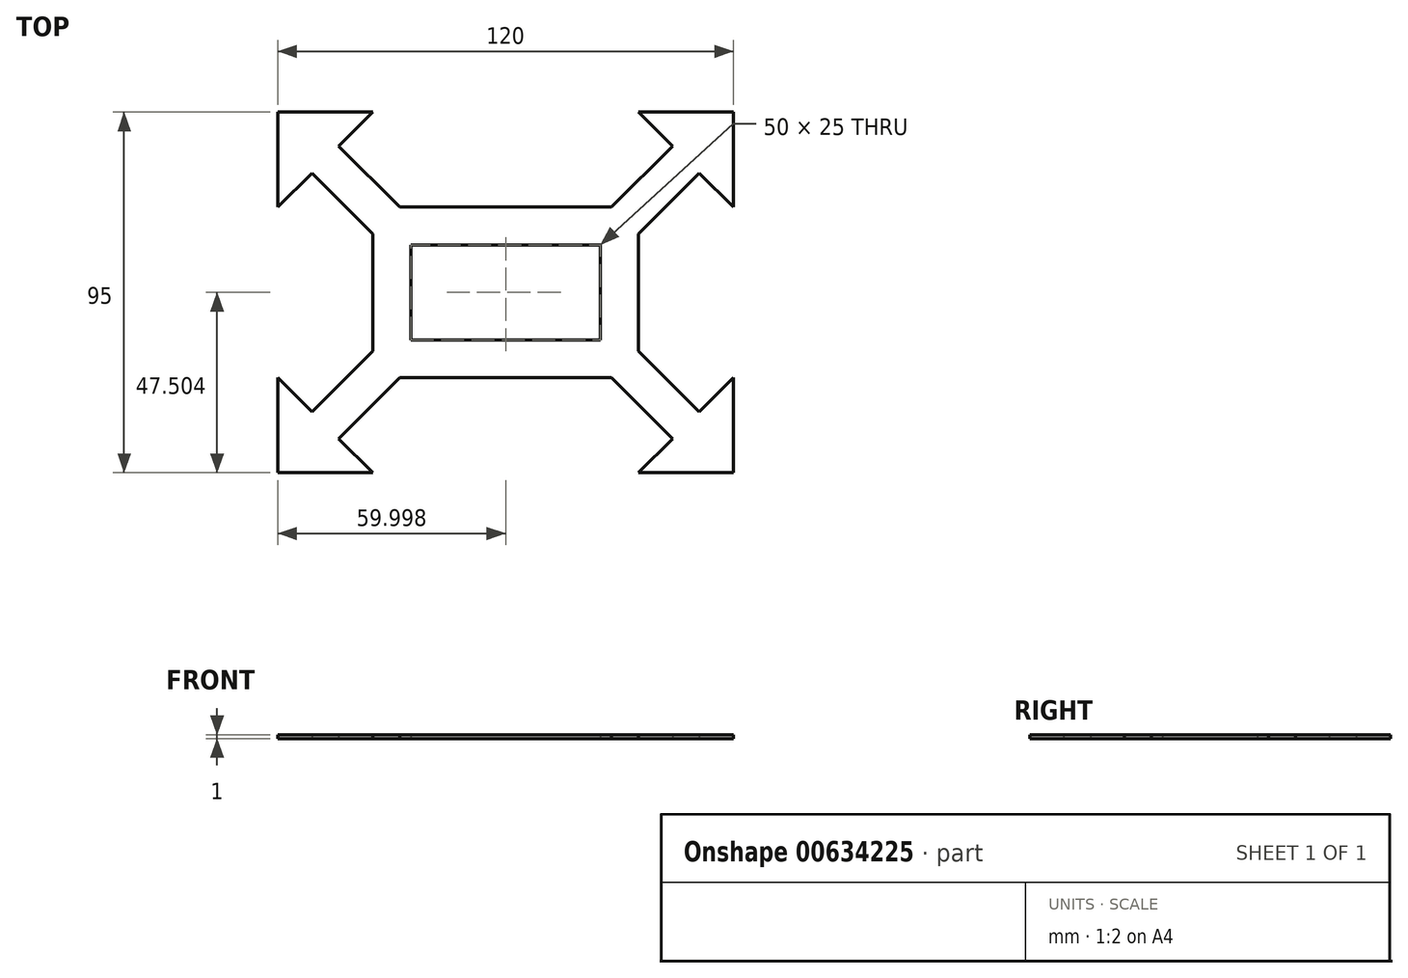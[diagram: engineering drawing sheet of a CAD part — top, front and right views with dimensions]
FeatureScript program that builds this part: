
annotation { "Feature Type Name" : "Feature", "Feature Type Description" : "" }
export const myFeature = defineFeature(function(context is Context, id is Id, definition is map)
    precondition{}
    {
        {
            var Q0;
            Q0=qCreatedBy(makeId("Top.planeOp"),FACE);
            var sketch = newSketch(context, id + "F0", { "sketchPlane" : qUnion([Q0])});
            skLineSegment(sketch, "E0.bottom", {"start": v(-26.4, 69.63) * mm, "end": v(-1.4, 69.63) * mm});
            skLineSegment(sketch, "E0.top", {"start": v(-26.4, -25.37) * mm, "end": v(-1.4, -25.37) * mm});
            skLineSegment(sketch, "E0.left", {"start": v(-26.4, 69.63) * mm, "end": v(-26.4, 44.63) * mm});
            skLineSegment(sketch, "E0.right", {"start": v(93.6, 69.63) * mm, "end": v(93.6, 44.63) * mm});
            skLineSegment(sketch, "E1", {"start": v(-26.4, 44.63) * mm, "end": v(-1.4, 69.63) * mm});
            skLineSegment(sketch, "E2.MirrorCS", {"start": v(93.6, 44.63) * mm, "end": v(68.6, 69.63) * mm});
            skLineSegment(sketch, "E3.MirrorCS", {"start": v(-26.4, 164.63) * mm, "end": v(-1.4, 139.63) * mm});
            skLineSegment(sketch, "E4.MirrorCS", {"start": v(-26.4, -0.37) * mm, "end": v(-1.4, -25.37) * mm});
            skLineSegment(sketch, "E5.MirrorCS", {"start": v(93.6, -0.37) * mm, "end": v(68.6, -25.37) * mm});
            skLineSegment(sketch, "E6", {"start": v(-1.4, 44.63) * mm, "end": v(-1.4, -0.37) * mm});
            skLineSegment(sketch, "E7", {"start": v(68.6, -0.37) * mm, "end": v(68.6, 44.63) * mm});
            skLineSegment(sketch, "E8", {"start": v(68.6, 44.63) * mm, "end": v(-1.4, 44.63) * mm});
            skLineSegment(sketch, "E9", {"start": v(-1.4, -0.37) * mm, "end": v(68.6, -0.37) * mm});
            skLineSegment(sketch, "E10.trimOffspring", {"start": v(-26.4, -0.37) * mm, "end": v(-26.4, -25.37) * mm});
            skLineSegment(sketch, "E11.trimOffspring", {"start": v(93.6, -0.37) * mm, "end": v(93.6, -25.37) * mm});
            skLineSegment(sketch, "E12.trimOffspring", {"start": v(68.6, 69.63) * mm, "end": v(93.6, 69.63) * mm});
            skLineSegment(sketch, "E13.trimOffspring", {"start": v(68.6, -25.37) * mm, "end": v(93.6, -25.37) * mm});
            skLineSegment(sketch, "E14.bottom", {"start": v(8.6, 34.63) * mm, "end": v(58.6, 34.63) * mm});
            skLineSegment(sketch, "E14.top", {"start": v(8.6, 9.63) * mm, "end": v(58.6, 9.63) * mm});
            skLineSegment(sketch, "E14.left", {"start": v(8.6, 34.63) * mm, "end": v(8.6, 9.63) * mm});
            skLineSegment(sketch, "E14.right", {"start": v(58.6, 34.63) * mm, "end": v(58.6, 9.63) * mm});
            skLineSegment(sketch, "E15", {"start": v(-10.37, -16.4) * mm, "end": v(5.67, -0.37) * mm});
            skLineSegment(sketch, "E16", {"start": v(77.56, -16.4) * mm, "end": v(61.53, -0.37) * mm});
            skLineSegment(sketch, "E17", {"start": v(84.63, 53.6) * mm, "end": v(68.6, 37.56) * mm});
            skLineSegment(sketch, "E18", {"start": v(-10.37, 60.67) * mm, "end": v(5.67, 44.63) * mm});
            skLineSegment(sketch, "E19.MirrorCS", {"start": v(-17.44, 53.6) * mm, "end": v(-1.4, 37.56) * mm});
            skLineSegment(sketch, "E20.MirrorCS", {"start": v(-17.44, -9.33) * mm, "end": v(-1.4, 6.7) * mm});
            skLineSegment(sketch, "E21.MirrorCS", {"start": v(84.63, -9.33) * mm, "end": v(68.6, 6.7) * mm});
            skLineSegment(sketch, "E22.MirrorCS", {"start": v(77.56, 60.67) * mm, "end": v(61.53, 44.63) * mm});
            skSolve(sketch);
        }
        {
            var Q0;
            Q0 = qSketchRegion(id + "F0", true);
            extrude(context, id + "F1", {"entities" : qUnion([Q0]), "depth" : 1 * mm, "offsetDistance" : 25 * mm});
        }
    });
